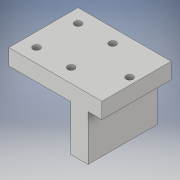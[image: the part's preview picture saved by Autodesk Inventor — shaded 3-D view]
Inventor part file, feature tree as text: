
AUTODESK INVENTOR PART (.ipt)
format: ipt  version: 2017 (Build 210142000, 142)  size: 139,264 bytes
history: native  units: in
note: dims shown in document units (in); Inventor stores cm internally (conversion verified against a paired STEP export)
features: sketch x4, extrude x2, hole x2
ambient origin geometry x8: Origin, YZ Plane, XZ Plane, XY Plane, X Axis, Y Axis, Z Axis, Center Point
bodies: Solid1 (feature_tree)
feature tree (8):
  extrude  "Extrusion1"  Depth=3.3625in
  extrude  "Extrusion3"  Depth=2.5in
  hole  "Hole1"  [1 undecoded]
  hole  "Hole2"  [1 undecoded]
  sketch  "Sketch1"  dims[d0=2.5in d1=3.3625in]
  sketch  "Sketch2"  dims[d2=0.575in d3=0.0in d4=2.5in]
  sketch  "Sketch4"  dims[d5=0.25in d6=0.5in]
  sketch  "Sketch5"  dims[d15=0.425in d16=0.425in d17=0.625in d18=0.625in d19=1.65in d20=0.0in d21=0.5in d22=0.5in d23=0.5in d24=0.5in d25=0.5in d26=0.5in d27=1.75in d28=1.75in d29=0.25in d30=0.75in d31=0.375in d32=0.25in d33=0.5635in d34=1.0in d35=0.8108in d36=0.25in d38=1.25in d39=0.25in d40=0.75in d41=0.375in d42=0.25in d43=0.5635in d44=1.0in d45=0.8108in]
note: 2 required parameter values undecoded (feature->parameter linkage not recoverable at this tier; creation-order binding heuristic only, values carry confidence <= 0.55)
